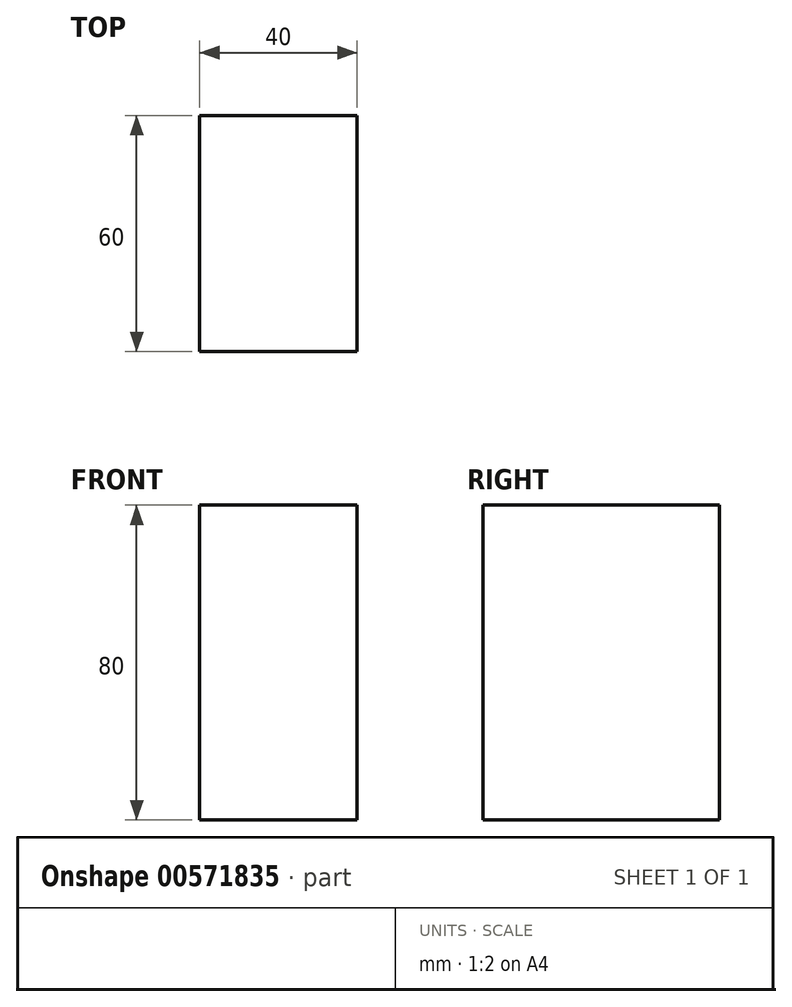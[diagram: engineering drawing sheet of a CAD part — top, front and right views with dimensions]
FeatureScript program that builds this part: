
annotation { "Feature Type Name" : "Feature", "Feature Type Description" : "" }
export const myFeature = defineFeature(function(context is Context, id is Id, definition is map)
    precondition{}
    {
        {
            var Q0;
            Q0=qCreatedBy(makeId("Top.planeOp"),FACE);
            var sketch = newSketch(context, id + "F0", { "sketchPlane" : qUnion([Q0])});
            skLineSegment(sketch, "E0.bottom", {"start": v(0, 0) * mm, "end": v(40, 0) * mm});
            skLineSegment(sketch, "E0.top", {"start": v(0, -60) * mm, "end": v(40, -60) * mm});
            skLineSegment(sketch, "E0.left", {"start": v(0, 0) * mm, "end": v(0, -60) * mm});
            skLineSegment(sketch, "E0.right", {"start": v(40, 0) * mm, "end": v(40, -60) * mm});
            skSolve(sketch);
        }
        {
            var Q0;
            Q0=makeQuery(id+"F0.imprint","IMPRINT",FACE,{"disambiguationData":[TD([[makeQuery(id+"F0.imprint","IMPRINT",EDGE,{"derivedFrom":sQuery(id+"F0.wireOp",EDGE,"E0.bottom")}),-1.0]])]});
            extrude(context, id + "F1", {"entities" : qUnion([Q0]), "depth" : 80 * mm, "offsetDistance" : 25 * mm});
        }
    });
